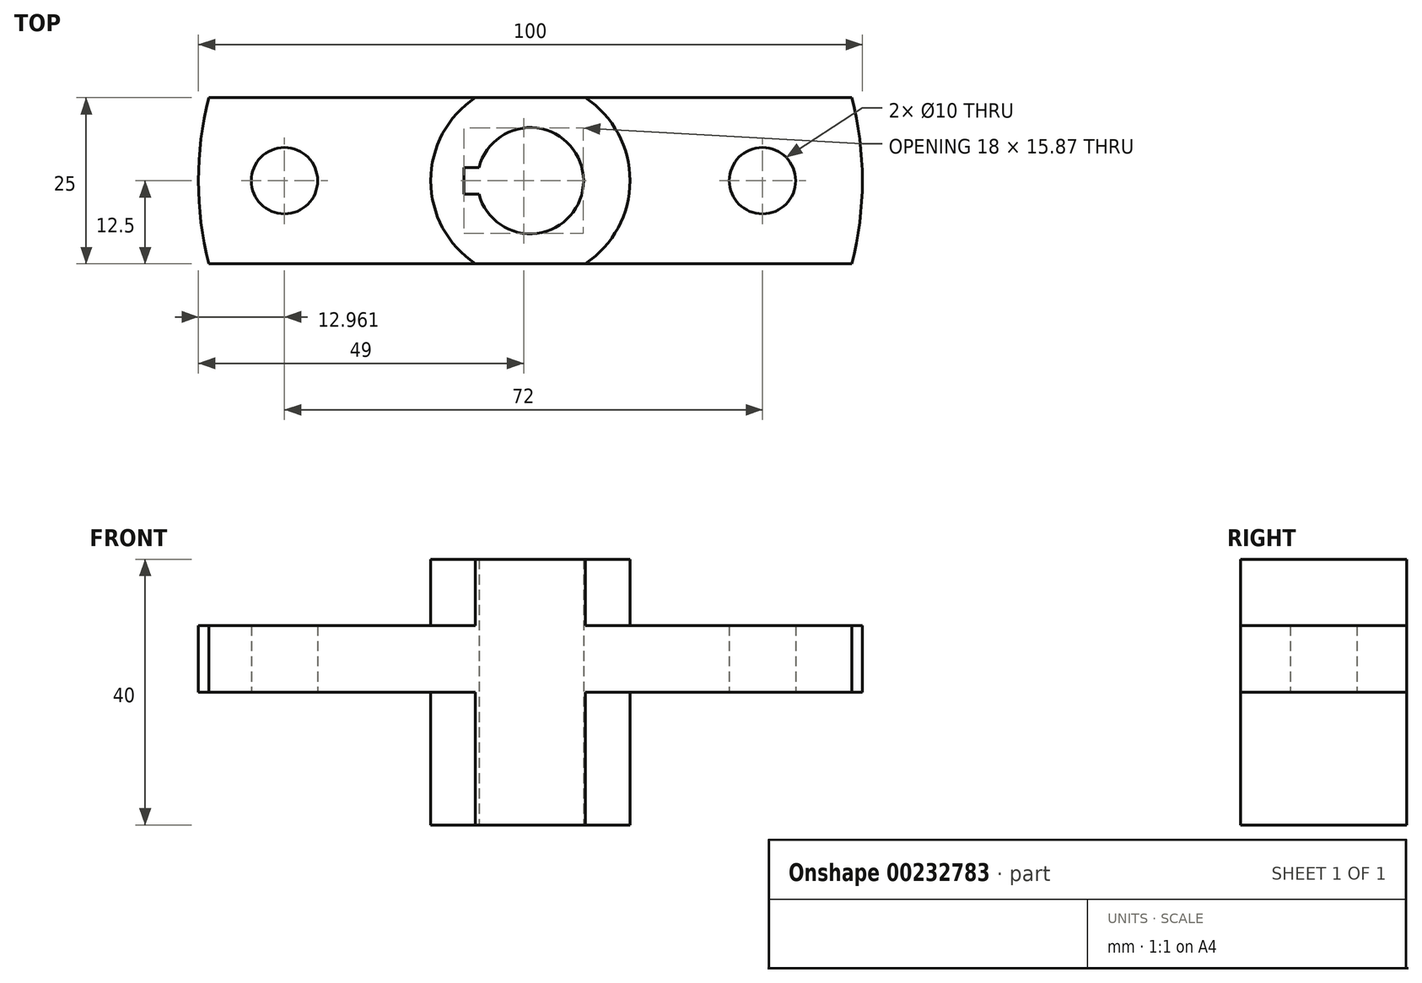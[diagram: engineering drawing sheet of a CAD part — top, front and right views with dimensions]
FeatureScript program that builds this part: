
annotation { "Feature Type Name" : "Feature", "Feature Type Description" : "" }
export const myFeature = defineFeature(function(context is Context, id is Id, definition is map)
    precondition{}
    {
        {
            var Q0;
            Q0=qCreatedBy(makeId("Top.planeOp"),FACE);
            var sketch = newSketch(context, id + "F0", { "sketchPlane" : qUnion([Q0])});
            skArc(sketch, "E0", {"start": v(-7.75, -2) * mm, "mid": v(8, 0) * mm, "end": v(-7.75, 2) * mm});
            skArc(sketch, "E1", {"start": v(-8.3, 12.5) * mm, "mid": v(-15, 0) * mm, "end": v(-8.3, -12.5) * mm});
            skLineSegment(sketch, "E2.bottom", {"start": v(-48.41, 12.5) * mm, "end": v(48.41, 12.5) * mm});
            skLineSegment(sketch, "E2.top", {"start": v(-48.41, -12.5) * mm, "end": v(48.41, -12.5) * mm});
            skArc(sketch, "E3", {"start": v(-48.41, 12.5) * mm, "mid": v(-50, 0) * mm, "end": v(-48.41, -12.5) * mm});
            skPoint(sketch, "E4.orphan", {"position": v(-50, 12.5) * mm});
            skPoint(sketch, "E5.orphan", {"position": v(-50, -12.5) * mm});
            skArc(sketch, "E6.trimOffspring", {"start": v(48.41, -12.5) * mm, "mid": v(50, 0) * mm, "end": v(48.41, 12.5) * mm});
            skPoint(sketch, "E7.orphan", {"position": v(50, -12.5) * mm});
            skPoint(sketch, "E8.orphan", {"position": v(50, 12.5) * mm});
            skArc(sketch, "E9.trimOffspring", {"start": v(8.3, -12.5) * mm, "mid": v(15, 0) * mm, "end": v(8.3, 12.5) * mm});
            skLineSegment(sketch, "E10.bottom", {"start": v(-10, 2) * mm, "end": v(-7.75, 2) * mm});
            skLineSegment(sketch, "E10.top", {"start": v(-10, -2) * mm, "end": v(-7.75, -2) * mm});
            skLineSegment(sketch, "E10.left", {"start": v(-10, 2) * mm, "end": v(-10, -2) * mm});
            skPoint(sketch, "E10.middle", {"position": v(-8, 0) * mm});
            skPoint(sketch, "E11.orphan", {"position": v(-6, 2) * mm});
            skPoint(sketch, "E12.orphan", {"position": v(-6, -2) * mm});
            skCircle(sketch, "E13", {"center": v(-37.04, 0) * mm, "radius": 5 * mm});
            skCircle(sketch, "E14", {"center": v(34.96, 0) * mm, "radius": 5 * mm});
            skSolve(sketch);
        }
        {
            var Q0;
            Q0=makeQuery(id+"F0.imprint","IMPRINT",FACE,{"disambiguationData":[TD([[makeQuery(id+"F0.imprint","IMPRINT",EDGE,{"derivedFrom":sQuery(id+"F0.wireOp",EDGE,"E0")}),-1.0]])]});
            extrude(context, id + "F1", {"entities" : qUnion([Q0]), "depth" : 20 * mm, "hasSecondDirection" : true, "secondDirectionOppositeDirection" : true, "secondDirectionDepth" : 20 * mm});
        }
        {
            var Q0;
            Q0 = qSketchRegion(id + "F0", true);
            extrude(context, id + "F2", {"entities" : qUnion([Q0]), "operationType" : NewBodyOperationType.ADD, "depth" : 10 * mm});
        }
    });
